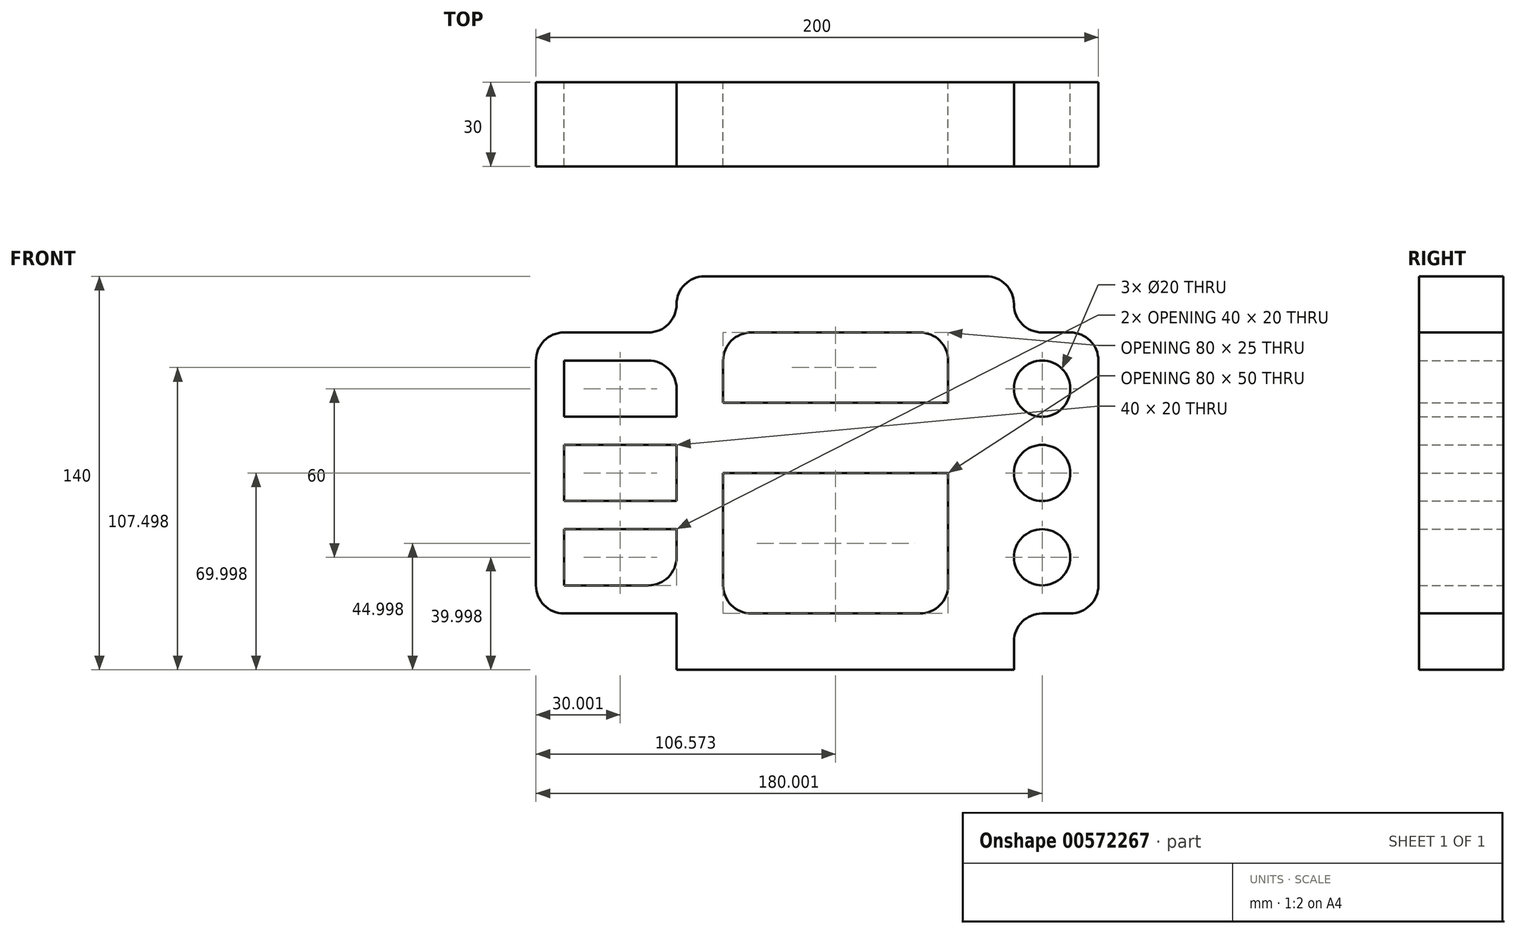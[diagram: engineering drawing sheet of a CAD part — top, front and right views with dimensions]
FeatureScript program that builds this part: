
annotation { "Feature Type Name" : "Feature", "Feature Type Description" : "" }
export const myFeature = defineFeature(function(context is Context, id is Id, definition is map)
    precondition{}
    {
        {
            var Q0;
            Q0=qCreatedBy(makeId("Front.planeOp"),FACE);
            var sketch = newSketch(context, id + "F0", { "sketchPlane" : qUnion([Q0])});
            skLineSegment(sketch, "E0", {"start": v(-57.56, -44.27) * mm, "end": v(62.44, -44.27) * mm});
            skLineSegment(sketch, "E1", {"start": v(-57.56, -44.27) * mm, "end": v(-57.56, -24.27) * mm});
            skLineSegment(sketch, "E2", {"start": v(-57.56, -24.27) * mm, "end": v(-97.56, -24.27) * mm});
            skLineSegment(sketch, "E3", {"start": v(-107.56, -14.27) * mm, "end": v(-107.56, 65.73) * mm});
            skPoint(sketch, "E4.visualSharp", {"position": v(-107.56, -24.27) * mm});
            skArc(sketch, "E4.filletArc", {"start": v(-107.56, -14.27) * mm, "mid": v(-104.63, -21.34) * mm, "end": v(-97.56, -24.27) * mm});
            skLineSegment(sketch, "E5", {"start": v(-97.56, 75.73) * mm, "end": v(-67.56, 75.73) * mm});
            skPoint(sketch, "E6.visualSharp", {"position": v(-107.56, 75.73) * mm});
            skArc(sketch, "E6.filletArc", {"start": v(-97.56, 75.73) * mm, "mid": v(-104.63, 72.8) * mm, "end": v(-107.56, 65.73) * mm});
            skLineSegment(sketch, "E7", {"start": v(-57.56, 85.73) * mm, "end": v(-57.56, 85.73) * mm});
            skPoint(sketch, "E8.visualSharp", {"position": v(-57.56, 75.73) * mm});
            skArc(sketch, "E8.filletArc", {"start": v(-67.56, 75.73) * mm, "mid": v(-60.49, 78.66) * mm, "end": v(-57.56, 85.73) * mm});
            skLineSegment(sketch, "E9", {"start": v(-47.56, 95.73) * mm, "end": v(52.44, 95.73) * mm});
            skPoint(sketch, "E10.visualSharp", {"position": v(-57.56, 95.73) * mm});
            skArc(sketch, "E10.filletArc", {"start": v(-47.56, 95.73) * mm, "mid": v(-54.63, 92.8) * mm, "end": v(-57.56, 85.73) * mm});
            skLineSegment(sketch, "E11", {"start": v(62.44, 85.73) * mm, "end": v(62.44, 85.73) * mm});
            skPoint(sketch, "E12.visualSharp", {"position": v(62.44, 95.73) * mm});
            skArc(sketch, "E12.filletArc", {"start": v(62.44, 85.73) * mm, "mid": v(59.51, 92.8) * mm, "end": v(52.44, 95.73) * mm});
            skLineSegment(sketch, "E13", {"start": v(72.44, 75.73) * mm, "end": v(82.44, 75.73) * mm});
            skPoint(sketch, "E14.visualSharp", {"position": v(62.44, 75.73) * mm});
            skArc(sketch, "E14.filletArc", {"start": v(62.44, 85.73) * mm, "mid": v(65.37, 78.66) * mm, "end": v(72.44, 75.73) * mm});
            skLineSegment(sketch, "E15", {"start": v(92.44, 65.73) * mm, "end": v(92.44, -14.27) * mm});
            skLineSegment(sketch, "E16", {"start": v(62.44, -44.27) * mm, "end": v(62.44, -34.27) * mm});
            skLineSegment(sketch, "E17", {"start": v(82.44, -24.27) * mm, "end": v(72.44, -24.27) * mm});
            skPoint(sketch, "E18.visualSharp", {"position": v(92.44, 75.73) * mm});
            skArc(sketch, "E18.filletArc", {"start": v(92.44, 65.73) * mm, "mid": v(89.51, 72.8) * mm, "end": v(82.44, 75.73) * mm});
            skPoint(sketch, "E19.visualSharp", {"position": v(92.44, -24.27) * mm});
            skArc(sketch, "E19.filletArc", {"start": v(82.44, -24.27) * mm, "mid": v(89.51, -21.34) * mm, "end": v(92.44, -14.27) * mm});
            skCircle(sketch, "E20", {"center": v(72.44, 25.73) * mm, "radius": 10 * mm});
            skCircle(sketch, "E21", {"center": v(72.44, 55.73) * mm, "radius": 10 * mm});
            skCircle(sketch, "E22", {"center": v(72.44, -4.27) * mm, "radius": 10 * mm});
            skPoint(sketch, "E23.visualSharp", {"position": v(62.44, -24.27) * mm});
            skArc(sketch, "E23.filletArc", {"start": v(72.44, -24.27) * mm, "mid": v(65.37, -27.2) * mm, "end": v(62.44, -34.27) * mm});
            skLineSegment(sketch, "E24.bottom", {"start": v(-30.99, 75.73) * mm, "end": v(29.01, 75.73) * mm});
            skLineSegment(sketch, "E24.top", {"start": v(-40.99, 50.73) * mm, "end": v(39.01, 50.73) * mm});
            skLineSegment(sketch, "E24.left", {"start": v(-40.99, 65.73) * mm, "end": v(-40.99, 50.73) * mm});
            skLineSegment(sketch, "E24.right", {"start": v(39.01, 65.73) * mm, "end": v(39.01, 50.73) * mm});
            skPoint(sketch, "E25.visualSharp", {"position": v(-40.99, 75.73) * mm});
            skArc(sketch, "E25.filletArc", {"start": v(-30.99, 75.73) * mm, "mid": v(-38.06, 72.8) * mm, "end": v(-40.99, 65.73) * mm});
            skPoint(sketch, "E26.visualSharp", {"position": v(39.01, 75.73) * mm});
            skArc(sketch, "E26.filletArc", {"start": v(39.01, 65.73) * mm, "mid": v(36.08, 72.8) * mm, "end": v(29.01, 75.73) * mm});
            skLineSegment(sketch, "E27.bottom", {"start": v(-40.99, 25.73) * mm, "end": v(39.01, 25.73) * mm});
            skLineSegment(sketch, "E27.top", {"start": v(-30.99, -24.27) * mm, "end": v(29.01, -24.27) * mm});
            skLineSegment(sketch, "E27.left", {"start": v(-40.99, 25.73) * mm, "end": v(-40.99, -14.27) * mm});
            skLineSegment(sketch, "E27.right", {"start": v(39.01, 25.73) * mm, "end": v(39.01, -14.27) * mm});
            skPoint(sketch, "E28.visualSharp", {"position": v(-40.99, -24.27) * mm});
            skArc(sketch, "E28.filletArc", {"start": v(-40.99, -14.27) * mm, "mid": v(-38.06, -21.34) * mm, "end": v(-30.99, -24.27) * mm});
            skPoint(sketch, "E29.visualSharp", {"position": v(39.01, -24.27) * mm});
            skArc(sketch, "E29.filletArc", {"start": v(29.01, -24.27) * mm, "mid": v(36.08, -21.34) * mm, "end": v(39.01, -14.27) * mm});
            skLineSegment(sketch, "E30.bottom", {"start": v(-97.56, 65.73) * mm, "end": v(-67.56, 65.73) * mm});
            skLineSegment(sketch, "E30.top", {"start": v(-97.56, 45.73) * mm, "end": v(-57.56, 45.73) * mm});
            skLineSegment(sketch, "E30.left", {"start": v(-97.56, 65.73) * mm, "end": v(-97.56, 45.73) * mm});
            skLineSegment(sketch, "E30.right", {"start": v(-57.56, 55.73) * mm, "end": v(-57.56, 45.73) * mm});
            skLineSegment(sketch, "E31.bottom", {"start": v(-97.56, 35.73) * mm, "end": v(-57.56, 35.73) * mm});
            skLineSegment(sketch, "E31.top", {"start": v(-97.56, 15.73) * mm, "end": v(-57.56, 15.73) * mm});
            skLineSegment(sketch, "E31.left", {"start": v(-97.56, 35.73) * mm, "end": v(-97.56, 15.73) * mm});
            skLineSegment(sketch, "E31.right", {"start": v(-57.56, 35.73) * mm, "end": v(-57.56, 15.73) * mm});
            skLineSegment(sketch, "E32.bottom", {"start": v(-97.56, 5.73) * mm, "end": v(-57.56, 5.73) * mm});
            skLineSegment(sketch, "E32.top", {"start": v(-97.56, -14.27) * mm, "end": v(-67.56, -14.27) * mm});
            skLineSegment(sketch, "E32.left", {"start": v(-97.56, 5.73) * mm, "end": v(-97.56, -14.27) * mm});
            skLineSegment(sketch, "E32.right", {"start": v(-57.56, 5.73) * mm, "end": v(-57.56, -4.27) * mm});
            skPoint(sketch, "E33.visualSharp", {"position": v(-57.56, 65.73) * mm});
            skArc(sketch, "E33.filletArc", {"start": v(-57.56, 55.73) * mm, "mid": v(-60.49, 62.8) * mm, "end": v(-67.56, 65.73) * mm});
            skPoint(sketch, "E34.visualSharp", {"position": v(-57.56, -14.27) * mm});
            skArc(sketch, "E34.filletArc", {"start": v(-67.56, -14.27) * mm, "mid": v(-60.49, -11.34) * mm, "end": v(-57.56, -4.27) * mm});
            skSolve(sketch);
        }
        {
            var Q0;
            Q0 = qSketchRegion(id + "F0", true);
            extrude(context, id + "F1", {"entities" : qUnion([Q0]), "depth" : 30 * mm, "offsetDistance" : 25 * mm});
        }
    });
